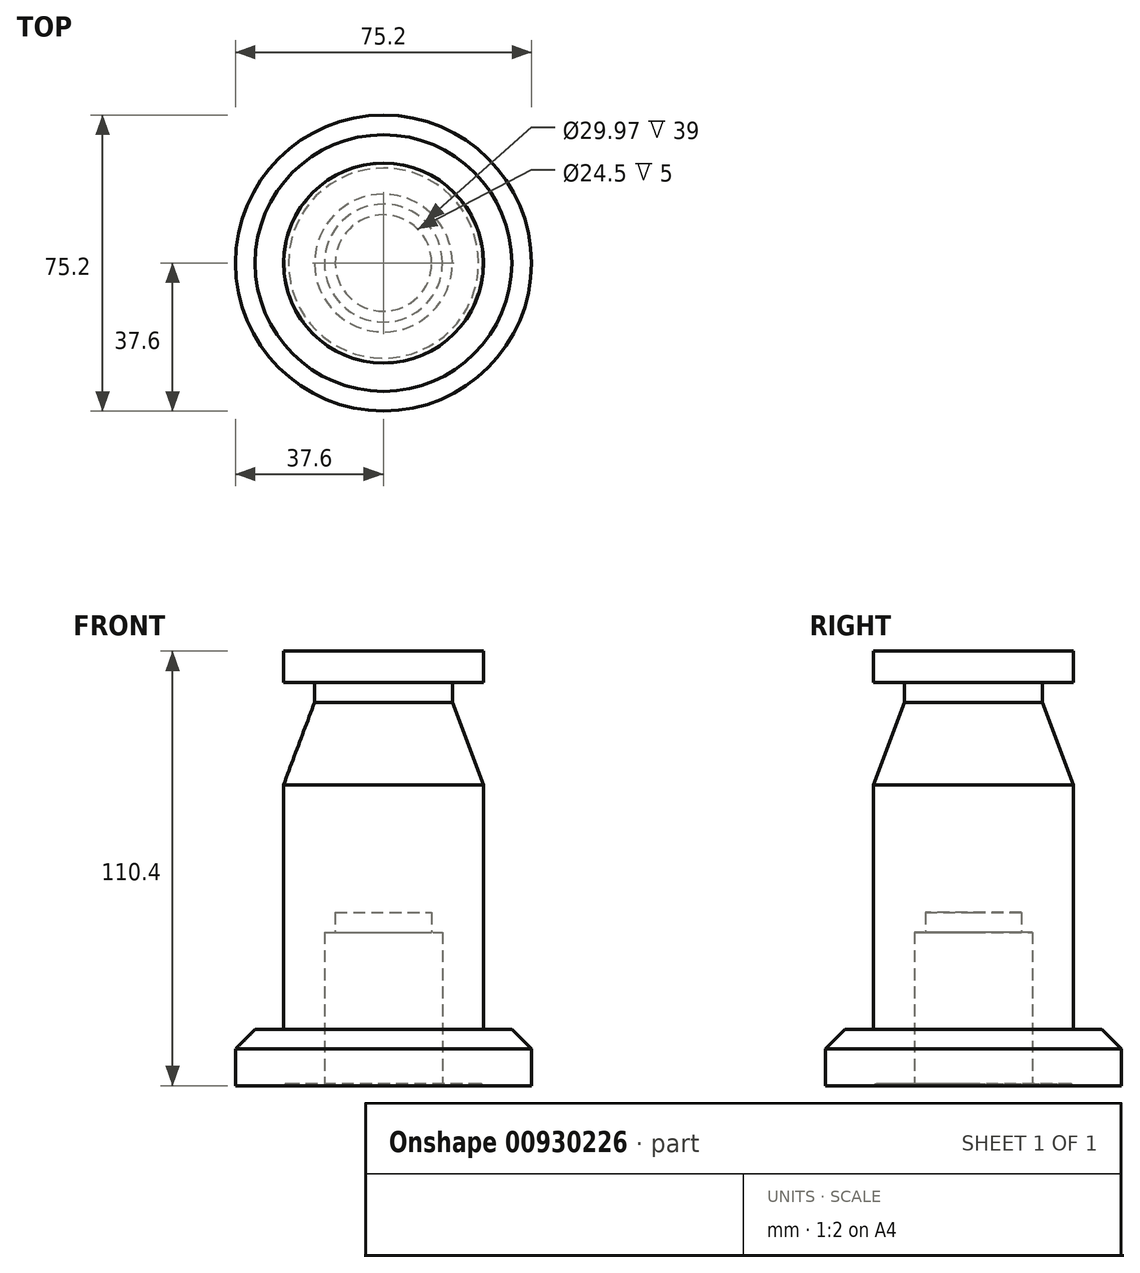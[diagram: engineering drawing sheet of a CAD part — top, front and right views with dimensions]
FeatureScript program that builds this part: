
annotation { "Feature Type Name" : "Feature", "Feature Type Description" : "" }
export const myFeature = defineFeature(function(context is Context, id is Id, definition is map)
    precondition{}
    {
        {
            var Q0;
            Q0=qCreatedBy(makeId("Front.planeOp"),FACE);
            var sketch = newSketch(context, id + "F0", { "sketchPlane" : qUnion([Q0])});
            skLineSegment(sketch, "E0", {"start": v(0, 0) * mm, "end": v(0, 125.25) * mm, "construction": true});
            skLineSegment(sketch, "E1", {"start": v(-37.6, 0) * mm, "end": v(-37.6, 9.3) * mm});
            skLineSegment(sketch, "E2", {"start": v(-37.6, 9.3) * mm, "end": v(-32.6, 14.3) * mm});
            skLineSegment(sketch, "E3", {"start": v(-32.6, 14.3) * mm, "end": v(-25.4, 14.3) * mm});
            skLineSegment(sketch, "E4", {"start": v(-25.4, 14.3) * mm, "end": v(-25.4, 76.4) * mm});
            skLineSegment(sketch, "E5", {"start": v(-25.4, 76.4) * mm, "end": v(-17.5, 97.4) * mm});
            skLineSegment(sketch, "E6", {"start": v(-17.5, 97.4) * mm, "end": v(-17.5, 102.4) * mm});
            skLineSegment(sketch, "E7", {"start": v(-17.5, 102.4) * mm, "end": v(-25.4, 102.4) * mm});
            skLineSegment(sketch, "E8", {"start": v(-25.4, 102.4) * mm, "end": v(-25.4, 110.4) * mm});
            skLineSegment(sketch, "E9", {"start": v(-25.4, 110.4) * mm, "end": v(0, 110.4) * mm});
            skLineSegment(sketch, "E10", {"start": v(-37.6, 0) * mm, "end": v(-25.15, 0) * mm});
            skLineSegment(sketch, "E11", {"start": v(-14.99, 0) * mm, "end": v(-14.99, 39) * mm});
            skLineSegment(sketch, "E12", {"start": v(-14.99, 39) * mm, "end": v(-12.25, 39) * mm});
            skLineSegment(sketch, "E13", {"start": v(-12.25, 39) * mm, "end": v(-12.25, 44) * mm});
            skLineSegment(sketch, "E14", {"start": v(-12.25, 44) * mm, "end": v(0, 44) * mm});
            skLineSegment(sketch, "E15", {"start": v(0, 44) * mm, "end": v(0, 110.4) * mm});
            skArc(sketch, "E16", {"start": v(-24.15, 0) * mm, "mid": v(-24.65, 0.5) * mm, "end": v(-25.15, 0) * mm});
            skLineSegment(sketch, "E17.trimOffspring", {"start": v(-24.15, 0) * mm, "end": v(-14.99, 0) * mm});
            skSolve(sketch);
        }
        {
            var Q0;
            Q0 = qSketchRegion(id + "F0", true);
            var Q1;
            Q1=sQuery(id+"F0.wireOp",EDGE,"E0");
            revolve(context, id + "F1", {"surfaceOperationType" : NewSurfaceOperationType.NEW, "entities" : qUnion([Q0]), "axis" : qUnion([Q1]), "revolveType" : RevolveType.FULL});
        }
    });
